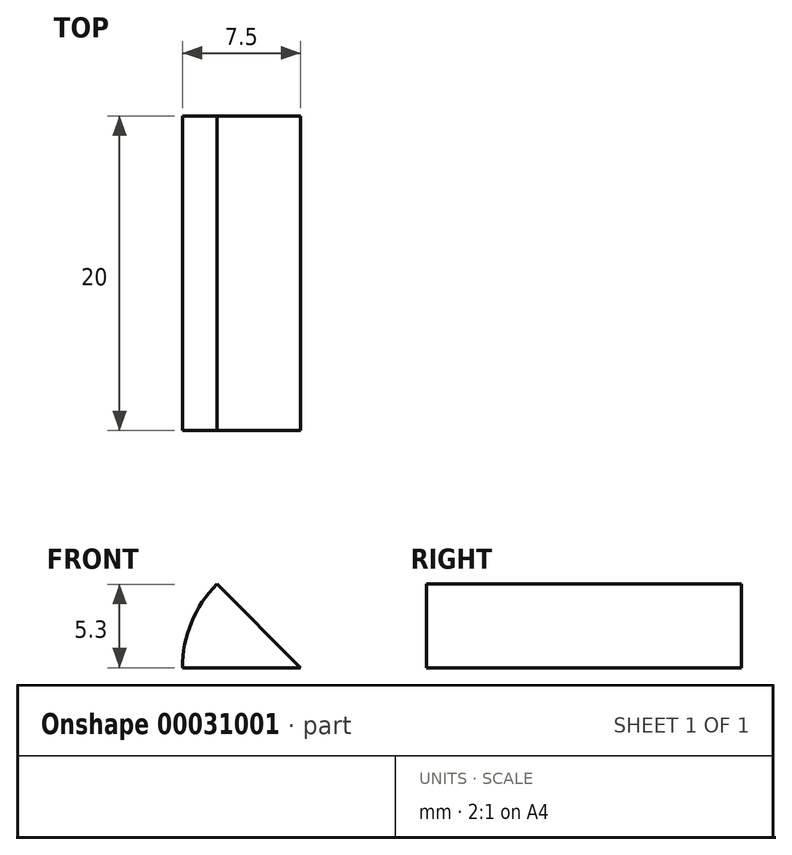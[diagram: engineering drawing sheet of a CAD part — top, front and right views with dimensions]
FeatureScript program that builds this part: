
annotation { "Feature Type Name" : "Feature", "Feature Type Description" : "" }
export const myFeature = defineFeature(function(context is Context, id is Id, definition is map)
    precondition{}
    {
        {
            var Q0;
            Q0=qCreatedBy(makeId("Front.planeOp"),FACE);
            var sketch = newSketch(context, id + "F0", { "sketchPlane" : qUnion([Q0])});
            skArc(sketch, "E0", {"start": v(-5.3, 5.3) * mm, "mid": v(-6.93, 2.87) * mm, "end": v(-7.5, 0) * mm});
            skLineSegment(sketch, "E1", {"start": v(-7.5, 0) * mm, "end": v(0, 0) * mm});
            skLineSegment(sketch, "E2", {"start": v(0, 0) * mm, "end": v(-5.3, 5.3) * mm});
            skPoint(sketch, "E3.orphan", {"position": v(0, 7.5) * mm});
            skSolve(sketch);
        }
        {
            var Q0;
            Q0 = qSketchRegion(id + "F0", true);
            extrude(context, id + "F1", {"entities" : qUnion([Q0]), "depth" : 20 * mm});
        }
    });
